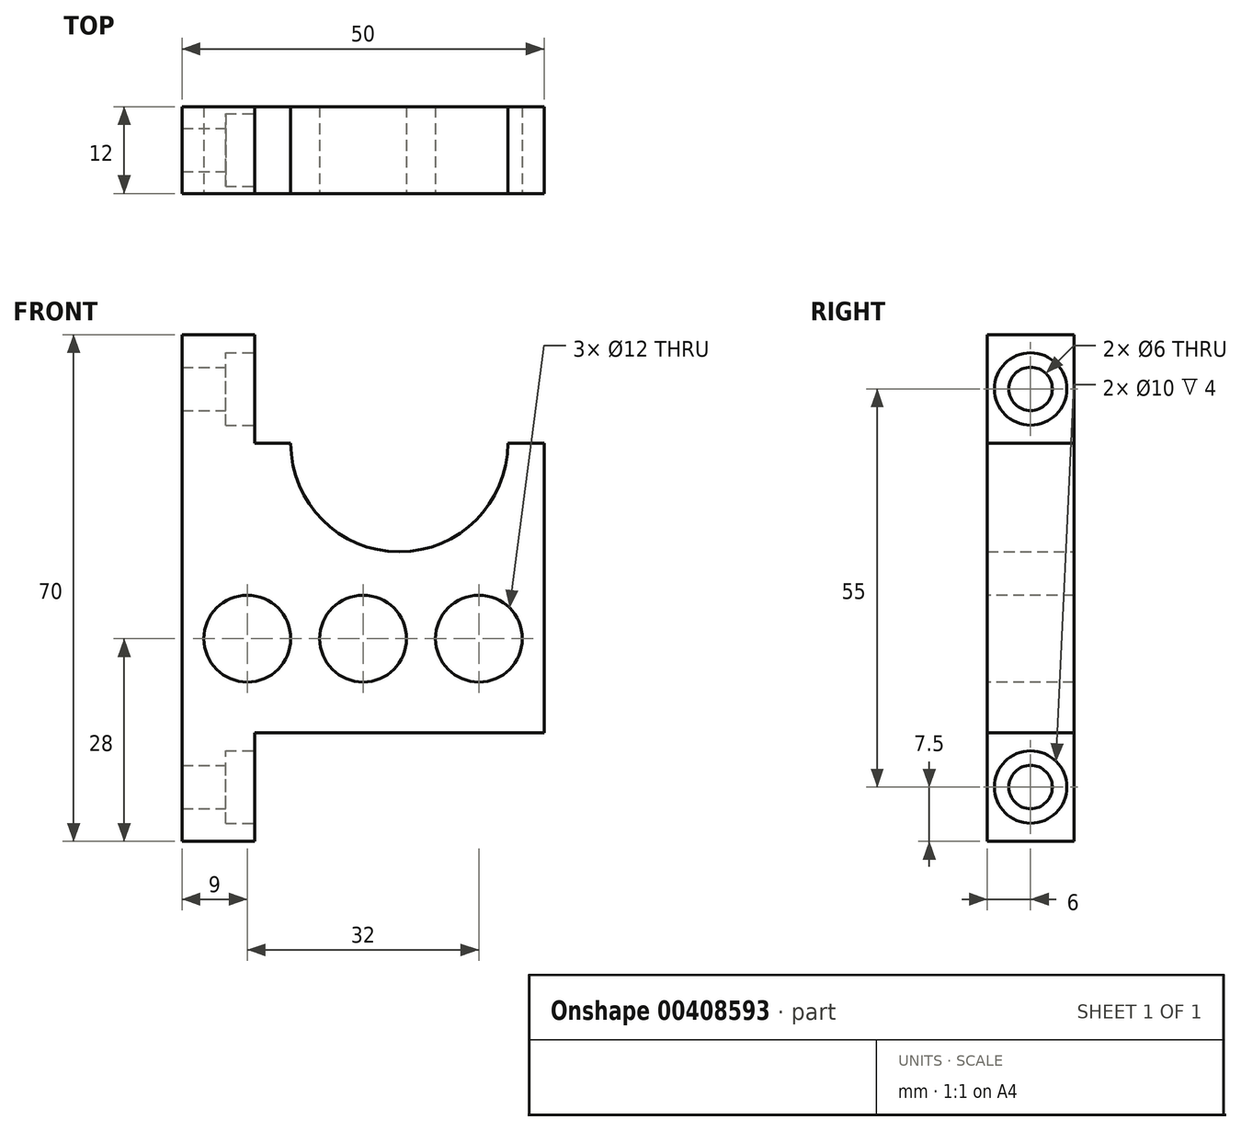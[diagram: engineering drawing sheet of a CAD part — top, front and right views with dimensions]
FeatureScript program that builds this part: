
annotation { "Feature Type Name" : "Feature", "Feature Type Description" : "" }
export const myFeature = defineFeature(function(context is Context, id is Id, definition is map)
    precondition{}
    {
        {
            var Q0;
            Q0=qCreatedBy(makeId("Front.planeOp"),FACE);
            var sketch = newSketch(context, id + "F0", { "sketchPlane" : qUnion([Q0])});
            skLineSegment(sketch, "E0.bottom", {"start": v(25, -35) * mm, "end": v(-25, -35) * mm});
            skLineSegment(sketch, "E0.top", {"start": v(25, 35) * mm, "end": v(-25, 35) * mm});
            skLineSegment(sketch, "E0.left", {"start": v(25, -35) * mm, "end": v(25, 35) * mm});
            skLineSegment(sketch, "E0.right", {"start": v(-25, -35) * mm, "end": v(-25, 35) * mm});
            skPoint(sketch, "E0.middle", {"position": v(0, 0) * mm});
            skPoint(sketch, "E1", {"position": v(5, 20) * mm});
            skCircle(sketch, "E2", {"center": v(5, 20) * mm, "radius": 15 * mm});
            skLineSegment(sketch, "E3", {"start": v(-15, 35) * mm, "end": v(-15, -35) * mm});
            skLineSegment(sketch, "E4", {"start": v(-25, 20) * mm, "end": v(25, 20) * mm});
            skLineSegment(sketch, "E5", {"start": v(-25, -20) * mm, "end": v(25, -20) * mm});
            skSolve(sketch);
        }
        {
            var Q0;
            {var subQ0=sQuery(id+"F0.wireOp",EDGE,"E0.right");var subQ1=sQuery(id+"F0.wireOp",EDGE,"E0.top");var subQ2=makeQuery(id+"F0.imprint","INTERSECT",VERTEX,{"derivedFrom":[subQ1,subQ0]});Q0=makeQuery(id+"F0.imprint","IMPRINT",FACE,{"disambiguationData":[TD([[makeQuery(id+"F0.imprint","IMPRINT",EDGE,{"disambiguationData":[TD([[subQ2,1.0]])],"derivedFrom":subQ1}),1.0]])]});}
            var Q1;
            {var subQ0=sQuery(id+"F0.wireOp",EDGE,"E4");var subQ1=sQuery(id+"F0.wireOp",EDGE,"E0.right");var subQ2=makeQuery(id+"F0.imprint","INTERSECT",VERTEX,{"derivedFrom":[subQ1,subQ0]});Q1=makeQuery(id+"F0.imprint","IMPRINT",FACE,{"disambiguationData":[TD([[makeQuery(id+"F0.imprint","IMPRINT",EDGE,{"disambiguationData":[TD([[subQ2,1.0]])],"derivedFrom":subQ1}),-1.0]])]});}
            var Q2;
            {var subQ0=sQuery(id+"F0.wireOp",EDGE,"E0.right");var subQ1=sQuery(id+"F0.wireOp",EDGE,"E0.bottom");var subQ2=makeQuery(id+"F0.imprint","INTERSECT",VERTEX,{"derivedFrom":[subQ1,subQ0]});Q2=makeQuery(id+"F0.imprint","IMPRINT",FACE,{"disambiguationData":[TD([[makeQuery(id+"F0.imprint","IMPRINT",EDGE,{"disambiguationData":[TD([[subQ2,1.0]])],"derivedFrom":subQ1}),-1.0]])]});}
            var Q3;
            {var subQ0=sQuery(id+"F0.wireOp",EDGE,"E4");var subQ8=sQuery(id+"F0.wireOp",EDGE,"E0.left");var subQ9=makeQuery(id+"F0.imprint","INTERSECT",VERTEX,{"derivedFrom":[subQ8,subQ0]});Q3=makeQuery(id+"F0.imprint","IMPRINT",FACE,{"disambiguationData":[TD([[makeQuery(id+"F0.imprint","IMPRINT",EDGE,{"disambiguationData":[TD([[subQ9,1.0]])],"derivedFrom":subQ8}),1.0]])]});}
            extrude(context, id + "F1", {"entities" : qUnion([Q0, Q1, Q2, Q3]), "depth" : 12 * mm});
        }
        {
            var Q0;
            {var subQ0=sQuery(id+"F0.wireOp",EDGE,"E3");Q0=makeQuery(id+"F1.opExtrude","SWEPT_FACE",FACE,{"disambiguationData":[OSD([subQ0]),TDD([makeQuery(id+"F0.imprint","IMPRINT",EDGE,{"disambiguationData":[TD([[makeQuery(id+"F0.imprint","INTERSECT",VERTEX,{"derivedFrom":[sQuery(id+"F0.wireOp",EDGE,"E0.top"),subQ0]}),-1.0]])],"derivedFrom":subQ0})])]});}
            var sketch = newSketch(context, id + "F2", { "sketchPlane" : qUnion([Q0])});
            skPoint(sketch, "E6", {"position": v(-6, 27.5) * mm});
            skCircle(sketch, "E7", {"center": v(-6, 27.5) * mm, "radius": 3 * mm});
            skCircle(sketch, "E8", {"center": v(-6, 27.5) * mm, "radius": 5 * mm});
            skSolve(sketch);
        }
        {
            var Q0;
            Q0=makeQuery(id+"F2.imprint","IMPRINT",FACE,{"disambiguationData":[TD([[makeQuery(id+"F2.imprint","IMPRINT",EDGE,{"derivedFrom":sQuery(id+"F2.wireOp",EDGE,"E7")}),1.0]])]});
            extrude(context, id + "F3", {"entities" : qUnion([Q0]), "operationType" : NewBodyOperationType.REMOVE, "endBound" : BoundingType.THROUGH_ALL, "oppositeDirection" : true, "depth" : 25 * mm});
        }
        {
            var Q0;
            {var subQ0=sQuery(id+"F0.wireOp",EDGE,"E3");Q0=makeQuery(id+"F1.opExtrude","SWEPT_FACE",FACE,{"disambiguationData":[OSD([subQ0]),TDD([makeQuery(id+"F0.imprint","IMPRINT",EDGE,{"disambiguationData":[TD([[makeQuery(id+"F0.imprint","INTERSECT",VERTEX,{"derivedFrom":[sQuery(id+"F0.wireOp",EDGE,"E0.top"),subQ0]}),-1.0]])],"derivedFrom":subQ0})])]});}
            var sketch = newSketch(context, id + "F4", { "sketchPlane" : qUnion([Q0])});
            skPoint(sketch, "E9", {"position": v(-6, 27.5) * mm});
            skCircle(sketch, "E10", {"center": v(-6, 27.5) * mm, "radius": 5 * mm});
            skSolve(sketch);
        }
        {
            var Q0;
            Q0=makeQuery(id+"F4.imprint","IMPRINT",FACE,{"disambiguationData":[TD([[makeQuery(id+"F4.imprint","IMPRINT",EDGE,{"derivedFrom":sQuery(id+"F4.wireOp",EDGE,"E10")}),1.0]])]});
            extrude(context, id + "F5", {"entities" : qUnion([Q0]), "operationType" : NewBodyOperationType.REMOVE, "oppositeDirection" : true, "depth" : 4 * mm});
        }
        {
            var Q0;
            {var subQ0=sQuery(id+"F0.wireOp",EDGE,"E3");Q0=makeQuery(id+"F1.opExtrude","SWEPT_FACE",FACE,{"disambiguationData":[OSD([subQ0]),TDD([makeQuery(id+"F0.imprint","IMPRINT",EDGE,{"disambiguationData":[TD([[makeQuery(id+"F0.imprint","INTERSECT",VERTEX,{"derivedFrom":[sQuery(id+"F0.wireOp",EDGE,"E0.bottom"),subQ0]}),1.0]])],"derivedFrom":subQ0})])]});}
            var sketch = newSketch(context, id + "F6", { "sketchPlane" : qUnion([Q0])});
            skPoint(sketch, "E11", {"position": v(-6, -27.5) * mm});
            skPoint(sketch, "E11.positionSnap0", {"position": v(-6, -35) * mm});
            skCircle(sketch, "E12", {"center": v(-6, -27.5) * mm, "radius": 3 * mm});
            skSolve(sketch);
        }
        {
            var Q0;
            Q0=makeQuery(id+"F6.imprint","IMPRINT",FACE,{"disambiguationData":[TD([[makeQuery(id+"F6.imprint","IMPRINT",EDGE,{"derivedFrom":sQuery(id+"F6.wireOp",EDGE,"E12")}),1.0]])]});
            extrude(context, id + "F7", {"entities" : qUnion([Q0]), "operationType" : NewBodyOperationType.REMOVE, "endBound" : BoundingType.THROUGH_ALL, "oppositeDirection" : true, "depth" : 25 * mm});
        }
        {
            var Q0;
            {var subQ0=sQuery(id+"F0.wireOp",EDGE,"E3");Q0=makeQuery(id+"F1.opExtrude","SWEPT_FACE",FACE,{"disambiguationData":[OSD([subQ0]),TDD([makeQuery(id+"F0.imprint","IMPRINT",EDGE,{"disambiguationData":[TD([[makeQuery(id+"F0.imprint","INTERSECT",VERTEX,{"derivedFrom":[sQuery(id+"F0.wireOp",EDGE,"E0.bottom"),subQ0]}),1.0]])],"derivedFrom":subQ0})])]});}
            var sketch = newSketch(context, id + "F8", { "sketchPlane" : qUnion([Q0])});
            skPoint(sketch, "E13", {"position": v(-6, -27.5) * mm});
            skCircle(sketch, "E14", {"center": v(-6, -27.5) * mm, "radius": 5 * mm});
            skSolve(sketch);
        }
        {
            var Q0;
            Q0=makeQuery(id+"F8.imprint","IMPRINT",FACE,{"disambiguationData":[TD([[makeQuery(id+"F8.imprint","IMPRINT",EDGE,{"derivedFrom":sQuery(id+"F8.wireOp",EDGE,"E14")}),1.0]])]});
            extrude(context, id + "F9", {"entities" : qUnion([Q0]), "operationType" : NewBodyOperationType.REMOVE, "oppositeDirection" : true, "depth" : 4 * mm});
        }
        {
            var Q0;
            Q0=makeQuery(id+"F1.opExtrude","CAP_FACE",FACE,{"disambiguationData":[OSD([sQuery(id+"F0.wireOp",EDGE,"E0.bottom"),sQuery(id+"F0.wireOp",EDGE,"E0.top"),sQuery(id+"F0.wireOp",EDGE,"E0.left"),sQuery(id+"F0.wireOp",EDGE,"E0.right"),sQuery(id+"F0.wireOp",EDGE,"E2"),sQuery(id+"F0.wireOp",EDGE,"E3"),sQuery(id+"F0.wireOp",EDGE,"E4"),sQuery(id+"F0.wireOp",EDGE,"E5")])],"isStart":false});
            var sketch = newSketch(context, id + "F10", { "sketchPlane" : qUnion([Q0])});
            skLineSegment(sketch, "E15", {"start": v(-25, -7) * mm, "end": v(25, -7) * mm});
            skPoint(sketch, "E16", {"position": v(0, -7) * mm});
            skPoint(sketch, "E17", {"position": v(16, -7) * mm});
            skPoint(sketch, "E18", {"position": v(-16, -7) * mm});
            skCircle(sketch, "E19", {"center": v(-16, -7) * mm, "radius": 6 * mm});
            skCircle(sketch, "E20", {"center": v(0, -7) * mm, "radius": 6 * mm});
            skCircle(sketch, "E21", {"center": v(16, -7) * mm, "radius": 6 * mm});
            skSolve(sketch);
        }
        {
            var Q0;
            {var subQ0=sQuery(id+"F10.wireOp",EDGE,"E19");var subQ1=sQuery(id+"F10.wireOp",EDGE,"E15");var subQ2=makeQuery(id+"F10.imprint","INTERSECT",VERTEX,{"disambiguationData":[OD(0.0)],"derivedFrom":[subQ1,subQ0]});Q0=makeQuery(id+"F10.imprint","IMPRINT",FACE,{"disambiguationData":[TD([[makeQuery(id+"F10.imprint","IMPRINT",EDGE,{"disambiguationData":[TD([[subQ2,-1.0]])],"derivedFrom":subQ1}),1.0]])]});}
            var Q1;
            {var subQ0=sQuery(id+"F10.wireOp",EDGE,"E19");var subQ1=sQuery(id+"F10.wireOp",EDGE,"E15");var subQ2=makeQuery(id+"F10.imprint","INTERSECT",VERTEX,{"disambiguationData":[OD(0.0)],"derivedFrom":[subQ1,subQ0]});Q1=makeQuery(id+"F10.imprint","IMPRINT",FACE,{"disambiguationData":[TD([[makeQuery(id+"F10.imprint","IMPRINT",EDGE,{"disambiguationData":[TD([[subQ2,-1.0]])],"derivedFrom":subQ1}),-1.0]])]});}
            var Q2;
            {var subQ0=sQuery(id+"F10.wireOp",EDGE,"E20");var subQ1=sQuery(id+"F10.wireOp",EDGE,"E15");var subQ2=makeQuery(id+"F10.imprint","INTERSECT",VERTEX,{"disambiguationData":[OD(0.0)],"derivedFrom":[subQ1,subQ0]});Q2=makeQuery(id+"F10.imprint","IMPRINT",FACE,{"disambiguationData":[TD([[makeQuery(id+"F10.imprint","IMPRINT",EDGE,{"disambiguationData":[TD([[subQ2,-1.0]])],"derivedFrom":subQ1}),1.0]])]});}
            var Q3;
            {var subQ0=sQuery(id+"F10.wireOp",EDGE,"E20");var subQ1=sQuery(id+"F10.wireOp",EDGE,"E15");var subQ2=makeQuery(id+"F10.imprint","INTERSECT",VERTEX,{"disambiguationData":[OD(0.0)],"derivedFrom":[subQ1,subQ0]});Q3=makeQuery(id+"F10.imprint","IMPRINT",FACE,{"disambiguationData":[TD([[makeQuery(id+"F10.imprint","IMPRINT",EDGE,{"disambiguationData":[TD([[subQ2,-1.0]])],"derivedFrom":subQ1}),-1.0]])]});}
            var Q4;
            {var subQ0=sQuery(id+"F10.wireOp",EDGE,"E21");var subQ1=sQuery(id+"F10.wireOp",EDGE,"E15");var subQ2=makeQuery(id+"F10.imprint","INTERSECT",VERTEX,{"disambiguationData":[OD(0.0)],"derivedFrom":[subQ1,subQ0]});Q4=makeQuery(id+"F10.imprint","IMPRINT",FACE,{"disambiguationData":[TD([[makeQuery(id+"F10.imprint","IMPRINT",EDGE,{"disambiguationData":[TD([[subQ2,-1.0]])],"derivedFrom":subQ1}),1.0]])]});}
            var Q5;
            {var subQ0=sQuery(id+"F10.wireOp",EDGE,"E21");var subQ1=sQuery(id+"F10.wireOp",EDGE,"E15");var subQ2=makeQuery(id+"F10.imprint","INTERSECT",VERTEX,{"disambiguationData":[OD(0.0)],"derivedFrom":[subQ1,subQ0]});Q5=makeQuery(id+"F10.imprint","IMPRINT",FACE,{"disambiguationData":[TD([[makeQuery(id+"F10.imprint","IMPRINT",EDGE,{"disambiguationData":[TD([[subQ2,-1.0]])],"derivedFrom":subQ1}),-1.0]])]});}
            extrude(context, id + "F11", {"entities" : qUnion([Q0, Q1, Q2, Q3, Q4, Q5]), "operationType" : NewBodyOperationType.REMOVE, "endBound" : BoundingType.THROUGH_ALL, "oppositeDirection" : true, "depth" : 25 * mm});
        }
    });
